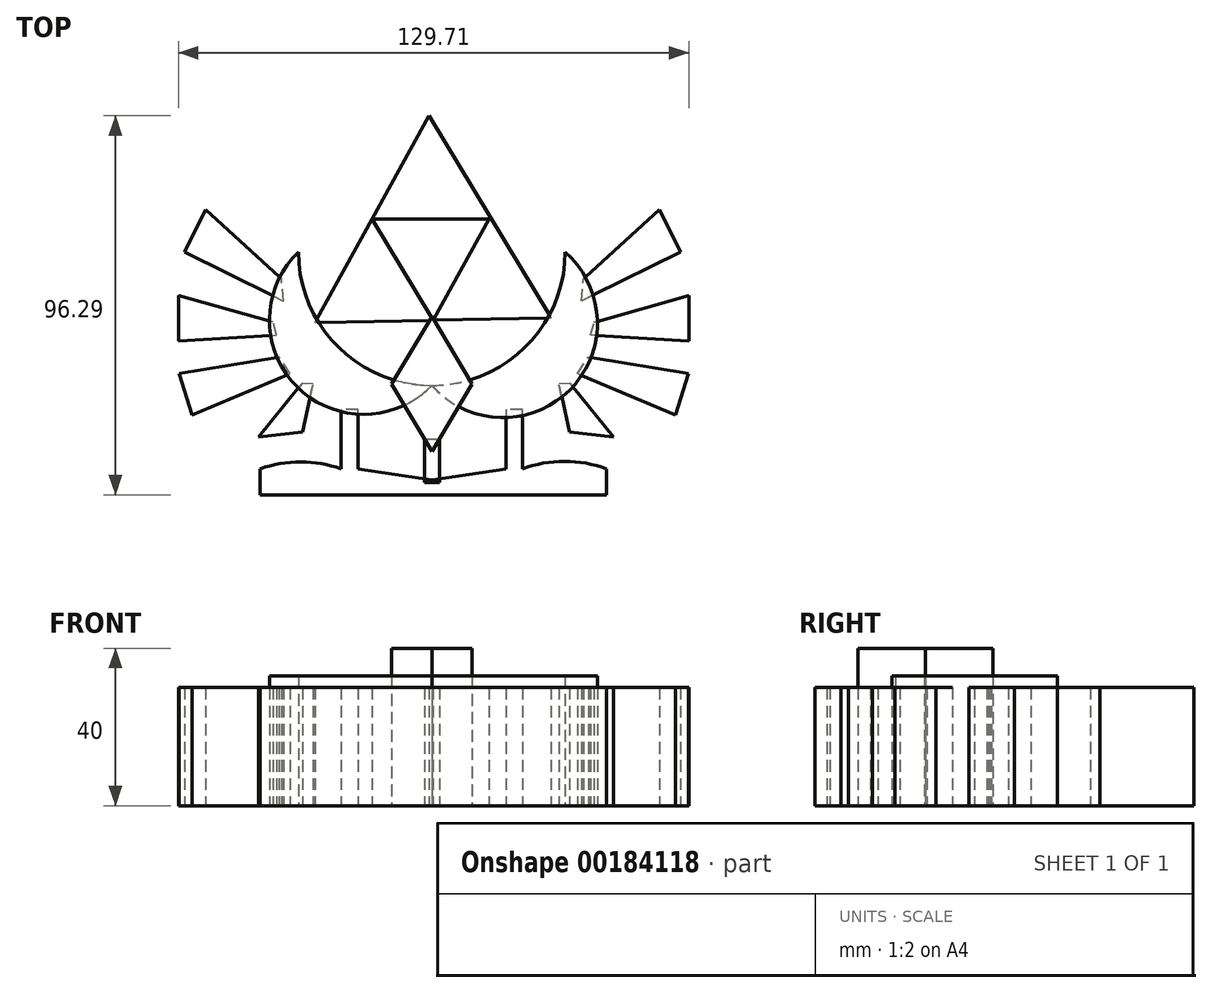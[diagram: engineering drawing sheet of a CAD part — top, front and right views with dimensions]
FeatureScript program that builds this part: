
annotation { "Feature Type Name" : "Feature", "Feature Type Description" : "" }
export const myFeature = defineFeature(function(context is Context, id is Id, definition is map)
    precondition{}
    {
        {
            var Q0;
            Q0=qCreatedBy(makeId("Top.planeOp"),FACE);
            var sketch = newSketch(context, id + "F0", { "sketchPlane" : qUnion([Q0])});
            skCircle(sketch, "E0.cCircle", {"center": v(0, 0) * mm, "radius": 17.32 * mm, "construction": true});
            skLineSegment(sketch, "E0.0", {"start": v(30.32, -16.75) * mm, "end": v(-29.67, -17.88) * mm});
            skLineSegment(sketch, "E0.1", {"start": v(-29.67, -17.88) * mm, "end": v(-0.65, 34.63) * mm});
            skLineSegment(sketch, "E0.2", {"start": v(-0.65, 34.63) * mm, "end": v(30.32, -16.75) * mm});
            skPoint(sketch, "E0.0.midPoint", {"position": v(0.32, -17.32) * mm});
            skLineSegment(sketch, "E1", {"start": v(0.32, -17.32) * mm, "end": v(-15.16, 8.38) * mm});
            skLineSegment(sketch, "E2", {"start": v(-15.16, 8.38) * mm, "end": v(14.83, 8.38) * mm});
            skPoint(sketch, "E2.endSnap0", {"position": v(14.83, 8.94) * mm});
            skLineSegment(sketch, "E3", {"start": v(14.83, 8.94) * mm, "end": v(0.32, -17.32) * mm});
            skSolve(sketch);
        }
        {
            var Q0;
            {var subQ0=sQuery(id+"F0.wireOp",EDGE,"E0.2");var subQ1=sQuery(id+"F0.wireOp",EDGE,"E0.1");var subQ2=makeQuery(id+"F0.imprint","INTERSECT",VERTEX,{"derivedFrom":[subQ1,subQ0]});Q0=makeQuery(id+"F0.imprint","IMPRINT",FACE,{"disambiguationData":[TD([[makeQuery(id+"F0.imprint","IMPRINT",EDGE,{"disambiguationData":[TD([[subQ2,-1.0]])],"derivedFrom":subQ0}),-1.0]])]});}
            var Q1;
            {var subQ3=sQuery(id+"F0.wireOp",EDGE,"E1");Q1=makeQuery(id+"F0.imprint","IMPRINT",FACE,{"disambiguationData":[TD([[makeQuery(id+"F0.imprint","IMPRINT",EDGE,{"derivedFrom":subQ3}),1.0]])]});}
            var Q2;
            {var subQ0=sQuery(id+"F0.wireOp",EDGE,"E0.2");var subQ1=sQuery(id+"F0.wireOp",EDGE,"E0.0");var subQ2=makeQuery(id+"F0.imprint","INTERSECT",VERTEX,{"derivedFrom":[subQ1,subQ0]});Q2=makeQuery(id+"F0.imprint","IMPRINT",FACE,{"disambiguationData":[TD([[makeQuery(id+"F0.imprint","IMPRINT",EDGE,{"disambiguationData":[TD([[subQ2,1.0]])],"derivedFrom":subQ0}),-1.0]])]});}
            extrude(context, id + "F1", {"entities" : qUnion([Q0, Q1, Q2]), "depth" : 30 * mm});
        }
        {
            var Q0;
            Q0=qCreatedBy(makeId("Top.planeOp"),FACE);
            var sketch = newSketch(context, id + "F2", { "sketchPlane" : qUnion([Q0])});
            skArc(sketch, "E4", {"start": v(-33.87, 0) * mm, "mid": v(-23.95, -23.95) * mm, "end": v(0, -33.87) * mm});
            skArc(sketch, "E5", {"start": v(0, -33.87) * mm, "mid": v(23.95, -23.95) * mm, "end": v(33.87, 0) * mm});
            skArc(sketch, "E6", {"start": v(-33.87, 0) * mm, "mid": v(-34.23, -34.23) * mm, "end": v(0, -33.87) * mm});
            skArc(sketch, "E7", {"start": v(0, -33.87) * mm, "mid": v(35.03, -35.03) * mm, "end": v(33.87, 0) * mm});
            skSolve(sketch);
        }
        {
            var Q0;
            Q0 = qSketchRegion(id + "F2", true);
            extrude(context, id + "F3", {"entities" : qUnion([Q0]), "depth" : 33 * mm});
        }
        {
            var Q0;
            Q0=qCreatedBy(makeId("Top.planeOp"),FACE);
            var sketch = newSketch(context, id + "F4", { "sketchPlane" : qUnion([Q0])});
            skLineSegment(sketch, "E8.2", {"start": v(0, -16.37) * mm, "end": v(10.24, -33.54) * mm});
            skPoint(sketch, "E8.0.midPoint", {"position": v(-5.57, -22.92) * mm});
            skLineSegment(sketch, "E9", {"start": v(0, -16.37) * mm, "end": v(-10.24, -33.54) * mm});
            skLineSegment(sketch, "E10", {"start": v(-10.24, -33.54) * mm, "end": v(0, -50.72) * mm});
            skLineSegment(sketch, "E11", {"start": v(0, -50.72) * mm, "end": v(10.24, -33.54) * mm});
            skSolve(sketch);
        }
        {
            var Q0;
            Q0 = qSketchRegion(id + "F4", true);
            extrude(context, id + "F5", {"entities" : qUnion([Q0]), "depth" : 40 * mm});
        }
        {
            var Q0;
            Q0=qCreatedBy(makeId("Top.planeOp"),FACE);
            var sketch = newSketch(context, id + "F6", { "sketchPlane" : qUnion([Q0])});
            skLineSegment(sketch, "E12", {"start": v(-38.24, -6.74) * mm, "end": v(-57.46, 10.76) * mm});
            skLineSegment(sketch, "E13", {"start": v(-57.46, 10.76) * mm, "end": v(-62.79, 0) * mm});
            skLineSegment(sketch, "E14", {"start": v(-62.79, 0) * mm, "end": v(-37.7, -12.42) * mm});
            skLineSegment(sketch, "E15", {"start": v(-37.7, -12.42) * mm, "end": v(-38.24, -6.74) * mm});
            skLineSegment(sketch, "E16", {"start": v(-57.46, 10.76) * mm, "end": v(-38.24, -6.74) * mm});
            skLineSegment(sketch, "E17", {"start": v(38.57, -6.74) * mm, "end": v(57.8, 10.76) * mm});
            skLineSegment(sketch, "E18", {"start": v(57.8, 10.76) * mm, "end": v(63.13, 0) * mm});
            skLineSegment(sketch, "E19", {"start": v(63.13, 0) * mm, "end": v(38.03, -12.42) * mm});
            skLineSegment(sketch, "E20", {"start": v(38.03, -12.42) * mm, "end": v(38.57, -6.74) * mm});
            skSolve(sketch);
        }
        {
            var Q0;
            Q0 = qSketchRegion(id + "F6", true);
            extrude(context, id + "F7", {"entities" : qUnion([Q0]), "depth" : 30 * mm});
        }
        {
            var Q0;
            Q0=qCreatedBy(makeId("Top.planeOp"),FACE);
            var sketch = newSketch(context, id + "F8", { "sketchPlane" : qUnion([Q0])});
            skLineSegment(sketch, "E21", {"start": v(-38.78, -26.68) * mm, "end": v(-64.23, -30.88) * mm});
            skLineSegment(sketch, "E22", {"start": v(-64.23, -30.88) * mm, "end": v(-60.93, -41.37) * mm});
            skLineSegment(sketch, "E23", {"start": v(-60.93, -41.37) * mm, "end": v(-36.06, -30.88) * mm});
            skLineSegment(sketch, "E24", {"start": v(-36.06, -30.88) * mm, "end": v(-38.78, -26.68) * mm});
            skLineSegment(sketch, "E25", {"start": v(39.77, -26.68) * mm, "end": v(65.22, -30.88) * mm});
            skLineSegment(sketch, "E26", {"start": v(65.22, -30.88) * mm, "end": v(61.93, -41.37) * mm});
            skLineSegment(sketch, "E27", {"start": v(61.93, -41.37) * mm, "end": v(37.05, -30.88) * mm});
            skLineSegment(sketch, "E28", {"start": v(37.05, -30.88) * mm, "end": v(39.77, -26.68) * mm});
            skLineSegment(sketch, "E29", {"start": v(-40.35, -17.81) * mm, "end": v(-64.4, -10.98) * mm});
            skLineSegment(sketch, "E30", {"start": v(-64.4, -10.98) * mm, "end": v(-64.4, -22.58) * mm});
            skLineSegment(sketch, "E31", {"start": v(-64.4, -22.58) * mm, "end": v(-39.44, -21.09) * mm});
            skLineSegment(sketch, "E32", {"start": v(-39.44, -21.09) * mm, "end": v(-40.35, -17.81) * mm});
            skLineSegment(sketch, "E33", {"start": v(41.26, -17.81) * mm, "end": v(65.3, -10.98) * mm});
            skLineSegment(sketch, "E34", {"start": v(65.3, -10.98) * mm, "end": v(65.3, -22.58) * mm});
            skLineSegment(sketch, "E35", {"start": v(65.3, -22.58) * mm, "end": v(40.35, -21.09) * mm});
            skLineSegment(sketch, "E36", {"start": v(40.35, -21.09) * mm, "end": v(41.26, -17.81) * mm});
            skSolve(sketch);
        }
        {
            var Q0;
            Q0 = qSketchRegion(id + "F8", true);
            extrude(context, id + "F9", {"entities" : qUnion([Q0]), "depth" : 30 * mm});
        }
        {
            var Q0;
            Q0=qCreatedBy(makeId("Top.planeOp"),FACE);
            var sketch = newSketch(context, id + "F10", { "sketchPlane" : qUnion([Q0])});
            skLineSegment(sketch, "E37", {"start": v(-32.85, -33.2) * mm, "end": v(-44.06, -47.02) * mm});
            skLineSegment(sketch, "E38", {"start": v(-44.06, -47.02) * mm, "end": v(-32.85, -45.65) * mm});
            skLineSegment(sketch, "E39", {"start": v(-32.85, -45.65) * mm, "end": v(-30.16, -33.45) * mm});
            skLineSegment(sketch, "E40", {"start": v(-32.85, -33.2) * mm, "end": v(-30.16, -33.45) * mm});
            skLineSegment(sketch, "E41", {"start": v(32.29, -33.45) * mm, "end": v(34.98, -33.2) * mm});
            skLineSegment(sketch, "E42", {"start": v(34.98, -33.2) * mm, "end": v(46.2, -47.02) * mm});
            skLineSegment(sketch, "E43", {"start": v(46.2, -47.02) * mm, "end": v(34.98, -45.65) * mm});
            skLineSegment(sketch, "E44", {"start": v(34.98, -45.65) * mm, "end": v(32.29, -33.45) * mm});
            skSolve(sketch);
        }
        {
            var Q0;
            Q0=makeQuery(id+"F10.imprint","IMPRINT",FACE,{"disambiguationData":[TD([[makeQuery(id+"F10.imprint","IMPRINT",EDGE,{"derivedFrom":sQuery(id+"F10.wireOp",EDGE,"E37")}),1.0]])]});
            var Q1;
            Q1=makeQuery(id+"F10.imprint","IMPRINT",FACE,{"disambiguationData":[TD([[makeQuery(id+"F10.imprint","IMPRINT",EDGE,{"derivedFrom":sQuery(id+"F10.wireOp",EDGE,"E41")}),-1.0]])]});
            extrude(context, id + "F11", {"entities" : qUnion([Q0, Q1]), "depth" : 30 * mm});
        }
        {
            var Q0;
            Q0=qCreatedBy(makeId("Top.planeOp"),FACE);
            var sketch = newSketch(context, id + "F12", { "sketchPlane" : qUnion([Q0])});
            skLineSegment(sketch, "E45", {"start": v(-23.02, -40.05) * mm, "end": v(-23.02, -55.05) * mm});
            skArc(sketch, "E46", {"start": v(-23.02, -55.05) * mm, "mid": v(-33.31, -53.32) * mm, "end": v(-43.6, -55.05) * mm});
            skLineSegment(sketch, "E47", {"start": v(-43.6, -55.05) * mm, "end": v(-43.6, -61.66) * mm});
            skLineSegment(sketch, "E48", {"start": v(-43.6, -61.66) * mm, "end": v(44.4, -61.66) * mm});
            skLineSegment(sketch, "E49", {"start": v(44.4, -61.66) * mm, "end": v(44.4, -55.05) * mm});
            skArc(sketch, "E50", {"start": v(44.4, -55.05) * mm, "mid": v(33.71, -53.18) * mm, "end": v(23.02, -55.05) * mm});
            skLineSegment(sketch, "E51", {"start": v(23.02, -55.05) * mm, "end": v(23.02, -40.05) * mm});
            skLineSegment(sketch, "E52", {"start": v(23.02, -40.05) * mm, "end": v(18.8, -40.05) * mm});
            skLineSegment(sketch, "E53", {"start": v(18.8, -40.05) * mm, "end": v(18.8, -55.05) * mm});
            skLineSegment(sketch, "E54", {"start": v(18.8, -55.05) * mm, "end": v(0, -57.85) * mm});
            skLineSegment(sketch, "E55", {"start": v(0, -57.85) * mm, "end": v(-18.8, -55.05) * mm});
            skLineSegment(sketch, "E56", {"start": v(-18.8, -55.05) * mm, "end": v(-18.8, -40.05) * mm});
            skLineSegment(sketch, "E57", {"start": v(-18.8, -40.05) * mm, "end": v(-23.02, -40.05) * mm});
            skSolve(sketch);
        }
        {
            var Q0;
            Q0 = qSketchRegion(id + "F12", true);
            extrude(context, id + "F13", {"entities" : qUnion([Q0]), "depth" : 30 * mm});
        }
        {
            var Q0;
            Q0=qCreatedBy(makeId("Top.planeOp"),FACE);
            var sketch = newSketch(context, id + "F14", { "sketchPlane" : qUnion([Q0])});
            skLineSegment(sketch, "E58", {"start": v(-1.83, -47.48) * mm, "end": v(1.95, -47.48) * mm});
            skLineSegment(sketch, "E59", {"start": v(1.95, -47.48) * mm, "end": v(1.95, -58.56) * mm});
            skLineSegment(sketch, "E60", {"start": v(1.95, -58.56) * mm, "end": v(-1.83, -58.56) * mm});
            skLineSegment(sketch, "E61", {"start": v(-1.83, -58.56) * mm, "end": v(-1.83, -47.48) * mm});
            skSolve(sketch);
        }
        {
            var Q0;
            Q0 = qSketchRegion(id + "F14", true);
            extrude(context, id + "F15", {"entities" : qUnion([Q0]), "depth" : 30 * mm});
        }
    });
